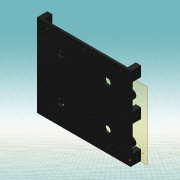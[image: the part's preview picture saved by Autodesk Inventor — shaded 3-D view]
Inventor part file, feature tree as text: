
AUTODESK INVENTOR PART (.ipt)
format: ipt  version: 2019 (Build 230136000, 136)  size: 311,808 bytes
history: native  units: mm
features: sketch x18, extrude x14, reference x8, fillet x3, other x2, plane x1
ambient origin geometry x8: Origin, YZ Plane, XZ Plane, XY Plane, X Axis, Y Axis, Z Axis, Center Point
bodies: Solid1 (feature_tree)
feature tree (46):
  plane  "Work Plane1"
  extrude  "Extrusion1"  Depth=8.0mm
  extrude  "Extrusion2"  Depth=8.0mm
  extrude  "Extrusion3"  Depth=10.0mm
  extrude  "Extrusion4"  Depth=1.5mm
  sketch  "Sketch5"  dims[d9=1.5mm d10=10.0mm d11=0.0mm]
  sketch  "Sketch6"  dims[d16=2.0mm d17=0.0mm d18=6.5mm d19=6.5mm]
  extrude  "Extrusion5"  Depth=10.0mm TaperAngle=0.0deg
  extrude  "Extrusion6"  Depth=2.0mm
  fillet  "Fillet1"  Radius=6.5mm
  extrude  "Extrusion7"  Depth=6.5mm
  extrude  "Extrusion8"  Depth=8.0mm
  fillet  "Fillet2"  Radius=10.0mm
  extrude  "Extrusion9"  Depth=5.0mm TaperAngle=0.0deg
  sketch  "Sketch12"  dims[d35=10.0mm d36=8.0mm]
  fillet  "Fillet3"  Radius=10.0mm
  extrude  "Extrusion10"  Depth=8.0mm
  extrude  "Extrusion11"  Depth=1.0mm
  extrude  "Extrusion12"  Depth=8.0mm
  extrude  "Extrusion13"  Depth=5.0mm TaperAngle=0.0deg
  extrude  "Extrusion14"  Depth=10.0mm
  sketch  "Sketch18"  dims[d47=1.5mm d48=5.0mm d49=8.0mm d50=10.0mm d51=5.0mm d52=0.0mm d53=1.0mm d56=1.5mm d57=5.0mm d58=8.0mm d59=10.0mm d60=8.0mm d61=5.0mm d62=0.0mm d63=1.5mm d65=8.0mm d66=10.0mm d67=8.0mm d68=5.0mm d69=0.0mm d70=8.0mm d71=10.0mm d73=1.5mm d74=5.0mm d75=0.0mm d76=5.0mm d77=0.0mm d79=2.5mm d83=2.5mm d85=2.5mm d86=2.0mm d87=0.0mm]
  sketch  "Sketch1"  dims[d0=8.0mm d1=8.0mm]
  reference  "Reference1"
  reference  "Reference2"
  reference  "Reference3"
  reference  "Reference4"
  sketch  "Sketch2"  dims[d2=8.0mm d3=8.0mm]
  sketch  "Sketch3"  dims[d4=10.0mm d5=0.0mm d6=1.5mm]
  reference  "Reference5"
  reference  "Reference6"
  reference  "Reference7"
  reference  "Reference8"
  sketch  "Sketch4"  dims[d7=1.5mm d8=1.5mm]
  sketch  "Sketch7"  dims[d20=6.5mm d21=6.5mm]
  sketch  "Sketch8"  dims[d22=2.0mm d23=0.0mm d24=8.0mm d25=10.0mm]
  sketch  "Sketch9"  dims[d26=1.5mm d27=5.0mm d28=0.0mm d29=10.0mm]
  sketch  "Sketch10"  dims[d30=8.0mm d31=1.5mm]
  sketch  "Sketch11"  dims[d32=5.0mm d33=0.0mm d34=1.0mm]
  sketch  "Sketch13"  dims[d37=1.5mm d38=5.0mm d39=0.0mm]
  sketch  "Sketch14"  dims[d40=8.0mm d41=10.0mm]
  sketch  "Sketch15"  dims[d42=1.5mm]
  sketch  "Sketch16"  dims[d43=5.0mm d44=0.0mm]
  sketch  "Sketch17"  dims[d45=1.0mm]
  other  "Ensamblaje Reloj LCD 16x2.iam"
  other  "PCB Down:1"
